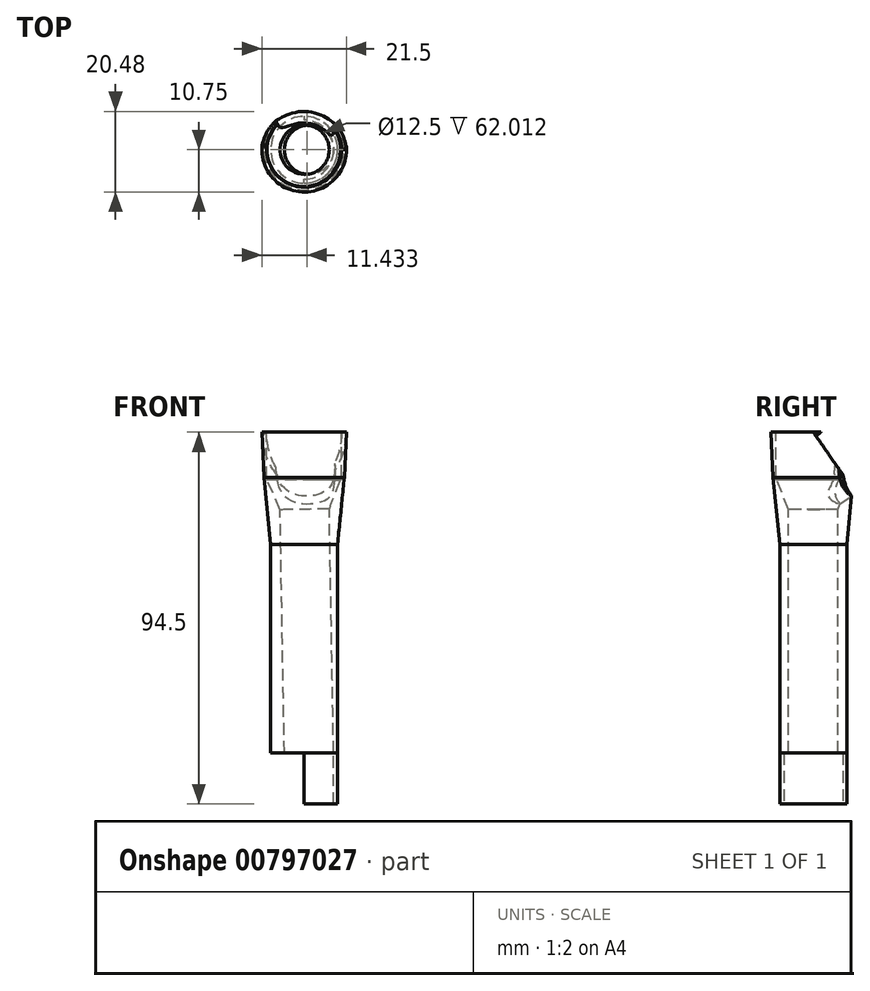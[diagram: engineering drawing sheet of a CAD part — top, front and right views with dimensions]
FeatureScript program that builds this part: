
annotation { "Feature Type Name" : "Feature", "Feature Type Description" : "" }
export const myFeature = defineFeature(function(context is Context, id is Id, definition is map)
    precondition{}
    {
        {
            var Q0;
            Q0=qCreatedBy(makeId("Front.planeOp"),FACE);
            var sketch = newSketch(context, id + "F0", { "sketchPlane" : qUnion([Q0])});
            skLineSegment(sketch, "E0", {"start": v(8.5, -17) * mm, "end": v(10.2, 0) * mm});
            skLineSegment(sketch, "E1", {"start": v(8.5, -17) * mm, "end": v(8.5, -70) * mm});
            skLineSegment(sketch, "E2", {"start": v(8.5, -70) * mm, "end": v(0, -70) * mm});
            skLineSegment(sketch, "E3", {"start": v(0, 0) * mm, "end": v(0, -70) * mm});
            skLineSegment(sketch, "E4", {"start": v(8.5, -70) * mm, "end": v(8.5, -83) * mm});
            skLineSegment(sketch, "E5", {"start": v(10.75, 11.5) * mm, "end": v(0, 11.5) * mm});
            skLineSegment(sketch, "E6", {"start": v(0, 11.5) * mm, "end": v(0, 0) * mm});
            skLineSegment(sketch, "E7", {"start": v(8.5, -70) * mm, "end": v(7.5, -70) * mm});
            skLineSegment(sketch, "E8", {"start": v(7.5, -70) * mm, "end": v(7.5, -83) * mm});
            skLineSegment(sketch, "E9", {"start": v(7.5, -83) * mm, "end": v(8.5, -83) * mm});
            skLineSegment(sketch, "E10", {"start": v(10.75, 11.5) * mm, "end": v(10.2, 0) * mm});
            skSolve(sketch);
        }
        {
            var Q0;
            Q0=makeQuery(id+"F0.imprint","IMPRINT",FACE,{"disambiguationData":[TD([[makeQuery(id+"F0.imprint","IMPRINT",EDGE,{"derivedFrom":sQuery(id+"F0.wireOp",EDGE,"E0")}),1.0]])]});
            var Q1;
            Q1=sQuery(id+"F0.wireOp",EDGE,"E3");
            revolve(context, id + "F1", {"surfaceOperationType" : NewSurfaceOperationType.NEW, "entities" : qUnion([Q0]), "axis" : qUnion([Q1]), "revolveType" : RevolveType.FULL});
        }
        {
            var Q0;
            Q0=makeQuery(id+"F0.imprint","IMPRINT",FACE,{"disambiguationData":[TD([[makeQuery(id+"F0.imprint","IMPRINT",EDGE,{"derivedFrom":sQuery(id+"F0.wireOp",EDGE,"E4")}),-1.0]])]});
            var Q1;
            Q1=sQuery(id+"F0.wireOp",EDGE,"E3");
            revolve(context, id + "F2", {"surfaceOperationType" : NewSurfaceOperationType.NEW, "entities" : qUnion([Q0]), "axis" : qUnion([Q1]), "revolveType" : RevolveType.SYMMETRIC, "angle" : 180 * degree});
        }
        {
            var Q0;
            Q0=qCreatedBy(makeId("Top.planeOp"),FACE);
            var Q1;
            Q1=sQuery(id+"F0.wireOp",VERTEX,"E5.end");
            cPlane(context, id + "F3", {"entities" : qUnion([Q0, Q1]), "cplaneType" : CPlaneType.PLANE_POINT, "offset" : 25 * mm, "width" : 150 * mm, "height" : 150 * mm});
        }
        {
            var Q0;
            Q0=qCreatedBy(id+"F3.planeOp",FACE);
            var sketch = newSketch(context, id + "F4", { "sketchPlane" : qUnion([Q0])});
            skPoint(sketch, "E11", {"position": v(0, 0) * mm});
            skLineSegment(sketch, "E12", {"start": v(-13.76, 0) * mm, "end": v(19.9, 0) * mm});
            skSolve(sketch);
        }
        {
            var Q0;
            Q0=sQuery(id+"F4.wireOp",VERTEX,"E11");
            var Q1;
            Q1=makeQuery(id+"F1.opRevolve","SWEPT_BODY",BODY,{"disambiguationData":[OSD([sQuery(id+"F0.wireOp",EDGE,"E0"),sQuery(id+"F0.wireOp",EDGE,"E1"),sQuery(id+"F0.wireOp",EDGE,"E2"),sQuery(id+"F0.wireOp",EDGE,"E3"),sQuery(id+"F0.wireOp",EDGE,"mXBFzC3B-eRyn-SNOT-b6eb-w5vjRN5BRS4y"),sQuery(id+"F0.wireOp",EDGE,"E5"),sQuery(id+"F0.wireOp",EDGE,"E6")])]});
            hole(context, id + "F5", {"style" : HoleStyle.SIMPLE, "endStyle" : HoleEndStyle.BLIND, "holeDiameter" : 19 * mm, "majorDiameter" : 5 * mm, "holeDepth" : 12 * mm, "isTappedThrough" : true, "tappedDepth" : 12 * mm, "tapClearance" : 3, "startFromSketch" : true, "locations" : qUnion([Q0]), "scope" : qUnion([Q1])});
        }
        {
            var Q0;
            Q0=qCreatedBy(makeId("Top.planeOp"),FACE);
            var Q1;
            Q1=sQuery(id+"F0.wireOp",VERTEX,"E3.start");
            cPlane(context, id + "F6", {"entities" : qUnion([Q0, Q1]), "cplaneType" : CPlaneType.PLANE_POINT, "offset" : 25 * mm, "width" : 150 * mm, "height" : 150 * mm});
        }
        {
            var Q0;
            Q0=qCreatedBy(makeId("Top.planeOp"),FACE);
            var sketch = newSketch(context, id + "F7", { "sketchPlane" : qUnion([Q0])});
            skLineSegment(sketch, "E13", {"start": v(0, 17.35) * mm, "end": v(0, -17.92) * mm});
            skSolve(sketch);
        }
        {
            var Q0;
            Q0=sQuery(id+"F7.wireOp",EDGE,"E13");
            var Q1;
            Q1=qCreatedBy(makeId("Top.planeOp"),FACE);
            cPlane(context, id + "F8", {"entities" : qUnion([Q0, Q1]), "cplaneType" : CPlaneType.LINE_ANGLE, "offset" : 25 * mm, "angle" : 1 * degree, "width" : 150 * mm, "height" : 150 * mm});
        }
        {
            var Q0;
            Q0=qCreatedBy(id+"F8.planeOp",FACE);
            var sketch = newSketch(context, id + "F9", { "sketchPlane" : qUnion([Q0])});
            skPoint(sketch, "E14", {"position": v(0, 0) * mm});
            skSolve(sketch);
        }
        {
            var Q0;
            Q0=sQuery(id+"F9.wireOp",VERTEX,"E14");
            var Q1;
            Q1=makeQuery(id+"F1.opRevolve","SWEPT_BODY",BODY,{"disambiguationData":[OSD([sQuery(id+"F0.wireOp",EDGE,"E0"),sQuery(id+"F0.wireOp",EDGE,"E1"),sQuery(id+"F0.wireOp",EDGE,"E2"),sQuery(id+"F0.wireOp",EDGE,"E3"),sQuery(id+"F0.wireOp",EDGE,"E5"),sQuery(id+"F0.wireOp",EDGE,"E6"),sQuery(id+"F0.wireOp",EDGE,"E7"),sQuery(id+"F0.wireOp",EDGE,"E10")])]});
            var Q2;
            Q2=makeQuery(id+"F2.opRevolve","SWEPT_BODY",BODY,{"disambiguationData":[OSD([sQuery(id+"F0.wireOp",EDGE,"E4"),sQuery(id+"F0.wireOp",EDGE,"E7"),sQuery(id+"F0.wireOp",EDGE,"E8"),sQuery(id+"F0.wireOp",EDGE,"E9")])]});
            hole(context, id + "F10", {"style" : HoleStyle.C_SINK, "endStyle" : HoleEndStyle.BLIND, "oppositeDirection" : true, "holeDiameter" : 12.5 * mm, "cSinkDiameter" : 19.2 * mm, "cSinkAngle" : 44.9 * degree, "majorDiameter" : 5 * mm, "holeDepth" : 71 * mm, "isTappedThrough" : true, "tappedDepth" : 12 * mm, "tapClearance" : 3, "startFromSketch" : true, "locations" : qUnion([Q0]), "scope" : qUnion([Q1, Q2])});
        }
        {
            var Q0;
            Q0=qCreatedBy(id+"F3.planeOp",FACE);
            var Q1;
            Q1=sQuery(id+"F0.wireOp",EDGE,"E5");
            cPlane(context, id + "F11", {"entities" : qUnion([Q0, Q1]), "cplaneType" : CPlaneType.LINE_ANGLE, "offset" : 25 * mm, "angle" : 55 * degree, "width" : 150 * mm, "height" : 150 * mm});
        }
        {
            var Q0;
            Q0=qCreatedBy(id+"F11.planeOp",FACE);
            var sketch = newSketch(context, id + "F12", { "sketchPlane" : qUnion([Q0])});
            skPoint(sketch, "E15", {"position": v(0.38, -1.96) * mm});
            skSolve(sketch);
        }
        {
            var Q0;
            Q0=sQuery(id+"F12.wireOp",VERTEX,"E15");
            var Q1;
            Q1=makeQuery(id+"F1.opRevolve","SWEPT_BODY",BODY,{"disambiguationData":[OSD([sQuery(id+"F0.wireOp",EDGE,"E0"),sQuery(id+"F0.wireOp",EDGE,"E1"),sQuery(id+"F0.wireOp",EDGE,"E2"),sQuery(id+"F0.wireOp",EDGE,"E3"),sQuery(id+"F0.wireOp",EDGE,"E5"),sQuery(id+"F0.wireOp",EDGE,"E6"),sQuery(id+"F0.wireOp",EDGE,"E7"),sQuery(id+"F0.wireOp",EDGE,"E10")])]});
            hole(context, id + "F13", {"style" : HoleStyle.SIMPLE, "endStyle" : HoleEndStyle.BLIND, "oppositeDirection" : true, "holeDiameter" : 15 * mm, "majorDiameter" : 5 * mm, "holeDepth" : 8 * mm, "isTappedThrough" : true, "tappedDepth" : 12 * mm, "tapClearance" : 3, "startFromSketch" : true, "locations" : qUnion([Q0]), "scope" : qUnion([Q1])});
        }
        {
            var Q0;
            Q0=sQuery(id+"F12.wireOp",VERTEX,"E15");
            var Q1;
            Q1=makeQuery(id+"F1.opRevolve","SWEPT_BODY",BODY,{"disambiguationData":[OSD([sQuery(id+"F0.wireOp",EDGE,"E0"),sQuery(id+"F0.wireOp",EDGE,"E1"),sQuery(id+"F0.wireOp",EDGE,"E2"),sQuery(id+"F0.wireOp",EDGE,"E3"),sQuery(id+"F0.wireOp",EDGE,"E5"),sQuery(id+"F0.wireOp",EDGE,"E6"),sQuery(id+"F0.wireOp",EDGE,"E7"),sQuery(id+"F0.wireOp",EDGE,"E10")])]});
            hole(context, id + "F14", {"style" : HoleStyle.SIMPLE, "endStyle" : HoleEndStyle.BLIND, "holeDiameter" : 30 * mm, "majorDiameter" : 5 * mm, "holeDepth" : 12 * mm, "isTappedThrough" : true, "tappedDepth" : 12 * mm, "tapClearance" : 3, "startFromSketch" : true, "locations" : qUnion([Q0]), "scope" : qUnion([Q1])});
        }
    });
